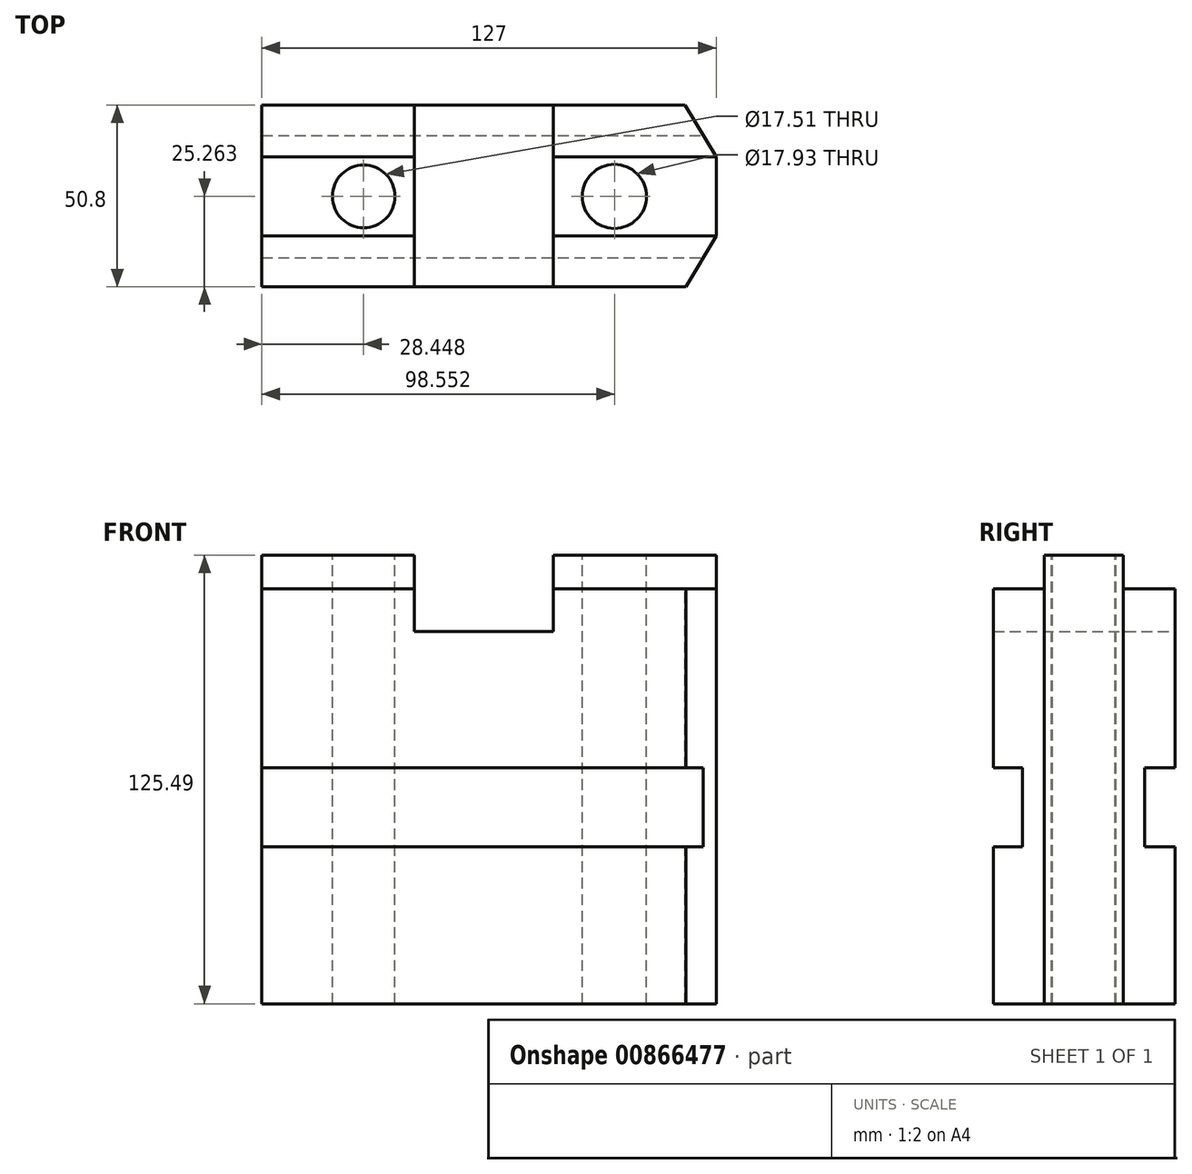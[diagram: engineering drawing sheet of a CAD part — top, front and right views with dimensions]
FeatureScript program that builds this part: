
annotation { "Feature Type Name" : "Feature", "Feature Type Description" : "" }
export const myFeature = defineFeature(function(context is Context, id is Id, definition is map)
    precondition{}
    {
        {
            var Q0;
            Q0=qCreatedBy(makeId("Right.planeOp"),FACE);
            var sketch = newSketch(context, id + "F0", { "sketchPlane" : qUnion([Q0])});
            skLineSegment(sketch, "E0", {"start": v(-42.3, 55.52) * mm, "end": v(-42.3, -60.54) * mm});
            skLineSegment(sketch, "E1", {"start": v(8.5, 55.52) * mm, "end": v(8.5, -60.54) * mm});
            skLineSegment(sketch, "E2", {"start": v(-42.3, 55.52) * mm, "end": v(8.5, 55.52) * mm});
            skLineSegment(sketch, "E3", {"start": v(-42.3, -60.54) * mm, "end": v(8.5, -60.54) * mm});
            skLineSegment(sketch, "E4", {"start": v(-42.3, 55.52) * mm, "end": v(-28.08, 55.52) * mm});
            skLineSegment(sketch, "E5", {"start": v(-28.08, 55.52) * mm, "end": v(-28.08, -60.54) * mm});
            skLineSegment(sketch, "E6", {"start": v(-5.98, 55.52) * mm, "end": v(-5.98, -60.54) * mm});
            skLineSegment(sketch, "E7", {"start": v(-28.08, 55.52) * mm, "end": v(-28.08, 64.95) * mm});
            skLineSegment(sketch, "E8", {"start": v(-5.98, 55.52) * mm, "end": v(-5.98, 64.95) * mm});
            skLineSegment(sketch, "E9", {"start": v(-5.98, 64.95) * mm, "end": v(-28.08, 64.95) * mm});
            skSolve(sketch);
        }
        {
            var Q0;
            {var subQ0=sQuery(id+"F0.wireOp",EDGE,"E7");var subQ1=sQuery(id+"F0.wireOp",EDGE,"E5");var subQ11=makeQuery(id+"F0.imprint","IMPRINT",EDGE,{"derivedFrom":subQ1});var subQ13=sQuery(id+"F0.wireOp",EDGE,"E1");var subQ14=sQuery(id+"F0.wireOp",EDGE,"E0");Q0=qUnion([makeQuery(id+"F0.imprint","IMPRINT",FACE,{"disambiguationData":[TD([[makeQuery(id+"F0.imprint","IMPRINT",EDGE,{"derivedFrom":subQ14}),1.0]])]}),makeQuery(id+"F0.imprint","IMPRINT",FACE,{"disambiguationData":[TD([[makeQuery(id+"F0.imprint","IMPRINT",EDGE,{"derivedFrom":subQ13}),-1.0]])]}),makeQuery(id+"F0.imprint","IMPRINT",FACE,{"disambiguationData":[TD([[makeQuery(id+"F0.imprint","IMPRINT",EDGE,{"derivedFrom":subQ0}),-1.0]])]}),makeQuery(id+"F0.imprint","IMPRINT",FACE,{"disambiguationData":[TD([[subQ11,1.0]])]})]);}
            extrude(context, id + "F1", {"entities" : qUnion([Q0]), "oppositeDirection" : true, "depth" : 127 * mm, "offsetDistance" : 25.4 * mm});
        }
        {
            var Q0;
            Q0=makeQuery(id+"F1.opExtrude","CAP_FACE",FACE,{"disambiguationData":[OSD([sQuery(id+"F0.wireOp",EDGE,"E0"),sQuery(id+"F0.wireOp",EDGE,"E1"),sQuery(id+"F0.wireOp",EDGE,"E2"),sQuery(id+"F0.wireOp",EDGE,"E3"),sQuery(id+"F0.wireOp",EDGE,"E7"),sQuery(id+"F0.wireOp",EDGE,"E8"),sQuery(id+"F0.wireOp",EDGE,"E9")])],"isStart":true});
            var sketch = newSketch(context, id + "F2", { "sketchPlane" : qUnion([Q0])});
            skLineSegment(sketch, "E10.bottom", {"start": v(8.5, 5.46) * mm, "end": v(0, 5.46) * mm});
            skLineSegment(sketch, "E10.top", {"start": v(8.5, -16.64) * mm, "end": v(0, -16.64) * mm});
            skLineSegment(sketch, "E10.left", {"start": v(8.5, 5.46) * mm, "end": v(8.5, -16.64) * mm});
            skLineSegment(sketch, "E10.right", {"start": v(0, 5.46) * mm, "end": v(0, -16.64) * mm});
            skLineSegment(sketch, "E11.bottom", {"start": v(-42.3, 5.46) * mm, "end": v(-34.2, 5.46) * mm});
            skLineSegment(sketch, "E11.top", {"start": v(-42.3, -16.64) * mm, "end": v(-34.2, -16.64) * mm});
            skLineSegment(sketch, "E11.left", {"start": v(-42.3, 5.46) * mm, "end": v(-42.3, -16.64) * mm});
            skLineSegment(sketch, "E11.right", {"start": v(-34.2, 5.46) * mm, "end": v(-34.2, -16.64) * mm});
            skSolve(sketch);
        }
        {
            var Q0;
            Q0=makeQuery(id+"F2.imprint","IMPRINT",FACE,{"disambiguationData":[TD([[makeQuery(id+"F2.imprint","IMPRINT",EDGE,{"derivedFrom":sQuery(id+"F2.wireOp",EDGE,"E10.bottom")}),1.0]])]});
            var Q1;
            Q1=makeQuery(id+"F2.imprint","IMPRINT",FACE,{"disambiguationData":[TD([[makeQuery(id+"F2.imprint","IMPRINT",EDGE,{"derivedFrom":sQuery(id+"F2.wireOp",EDGE,"E11.bottom")}),-1.0]])]});
            extrude(context, id + "F3", {"entities" : qUnion([Q0, Q1]), "operationType" : NewBodyOperationType.REMOVE, "oppositeDirection" : true, "depth" : 254 * mm, "offsetDistance" : 25.4 * mm});
        }
        {
            var Q0;
            Q0=makeQuery(id+"F1.opExtrude","SWEPT_FACE",FACE,{"disambiguationData":[OSD([sQuery(id+"F0.wireOp",EDGE,"E9")])]});
            var sketch = newSketch(context, id + "F4", { "sketchPlane" : qUnion([Q0])});
            skCircle(sketch, "E12", {"center": v(-98.55, -17.03) * mm, "radius": 8.76 * mm});
            skPoint(sketch, "E12.centerSnap0", {"position": v(-127, -17.03) * mm});
            skCircle(sketch, "E13", {"center": v(-28.45, -17.03) * mm, "radius": 8.97 * mm});
            skPoint(sketch, "E13.centerSnap0", {"position": v(0, -17.03) * mm});
            skSolve(sketch);
        }
        {
            var Q0;
            Q0=makeQuery(id+"F4.imprint","IMPRINT",FACE,{"disambiguationData":[TD([[makeQuery(id+"F4.imprint","IMPRINT",EDGE,{"derivedFrom":sQuery(id+"F4.wireOp",EDGE,"E13")}),1.0]])]});
            var Q1;
            Q1=makeQuery(id+"F4.imprint","IMPRINT",FACE,{"disambiguationData":[TD([[makeQuery(id+"F4.imprint","IMPRINT",EDGE,{"derivedFrom":sQuery(id+"F4.wireOp",EDGE,"E12")}),1.0]])]});
            extrude(context, id + "F5", {"entities" : qUnion([Q0, Q1]), "operationType" : NewBodyOperationType.REMOVE, "oppositeDirection" : true, "depth" : 231.14 * mm, "offsetDistance" : 25.4 * mm});
        }
        {
            var Q0;
            {var subQ5=sQuery(id+"F0.wireOp",EDGE,"E1");Q0=makeQuery(id+"F3.boolean.opBoolean","SPLIT",FACE,{"disambiguationData":[TD([makeQuery(id+"F3.opExtrude","SWEPT_FACE",FACE,{"disambiguationData":[OSD([sQuery(id+"F2.wireOp",EDGE,"E10.bottom")])]})])],"derivedFrom":makeQuery(id+"F1.opExtrude","SWEPT_FACE",FACE,{"disambiguationData":[OSD([subQ5])]})});}
            var sketch = newSketch(context, id + "F6", { "sketchPlane" : qUnion([Q0])});
            skLineSegment(sketch, "E14", {"start": v(63.5, 5.46) * mm, "end": v(63.5, 30.86) * mm});
            skLineSegment(sketch, "E15", {"start": v(45.5, 55.52) * mm, "end": v(45.5, 30.86) * mm});
            skLineSegment(sketch, "E16", {"start": v(45.5, 30.86) * mm, "end": v(65.36, 30.86) * mm});
            skLineSegment(sketch, "E17", {"start": v(65.36, 30.86) * mm, "end": v(84.41, 30.86) * mm});
            skLineSegment(sketch, "E18", {"start": v(84.41, 30.86) * mm, "end": v(84.41, 55.52) * mm});
            skLineSegment(sketch, "E19", {"start": v(84.41, 55.52) * mm, "end": v(45.5, 55.52) * mm});
            skSolve(sketch);
        }
        {
            var Q0;
            {var subQ3=sQuery(id+"F6.wireOp",EDGE,"E15");Q0=makeQuery(id+"F6.imprint","IMPRINT",FACE,{"disambiguationData":[TD([[makeQuery(id+"F6.imprint","IMPRINT",EDGE,{"derivedFrom":subQ3}),1.0]])]});}
            extrude(context, id + "F7", {"entities" : qUnion([Q0]), "operationType" : NewBodyOperationType.REMOVE, "oppositeDirection" : true, "depth" : 127 * mm, "offsetDistance" : 25.4 * mm});
        }
        {
            var Q0;
            Q0=makeQuery(id+"F1.opExtrude","SWEPT_FACE",FACE,{"disambiguationData":[OSD([sQuery(id+"F0.wireOp",EDGE,"E8")])]});
            var sketch = newSketch(context, id + "F8", { "sketchPlane" : qUnion([Q0])});
            skLineSegment(sketch, "E20", {"start": v(45.5, 55.52) * mm, "end": v(45.5, 64.95) * mm});
            skLineSegment(sketch, "E21", {"start": v(45.5, 64.95) * mm, "end": v(84.41, 64.95) * mm});
            skLineSegment(sketch, "E22", {"start": v(84.41, 64.95) * mm, "end": v(84.41, 55.52) * mm});
            skSolve(sketch);
        }
        {
            var Q0;
            Q0 = qSketchRegion(id + "F8", true);
            var Q1;
            Q1=makeQuery(id+"F8.imprint","IMPRINT",FACE,{"disambiguationData":[TD([[makeQuery(id+"F8.imprint","IMPRINT",EDGE,{"derivedFrom":sQuery(id+"F8.wireOp",EDGE,"E20")}),-1.0]])]});
            extrude(context, id + "F9", {"entities" : qUnion([Q0, Q1]), "operationType" : NewBodyOperationType.REMOVE, "oppositeDirection" : true, "depth" : 50.8 * mm, "offsetDistance" : 25.4 * mm});
        }
        {
            var Q0;
            Q0=makeQuery(id+"F7.boolean.opBoolean","COPY",FACE,{"derivedFrom":makeQuery(id+"F7.opExtrude","SWEPT_FACE",FACE,{"disambiguationData":[OSD([sQuery(id+"F6.wireOp",EDGE,"E16"),sQuery(id+"F6.wireOp",EDGE,"E17")])]})});
            var sketch = newSketch(context, id + "F10", { "sketchPlane" : qUnion([Q0])});
            skSolve(sketch);
        }
        {
            var Q0;
            Q0 = qSketchRegion(id + "F10", true);
            var Q1;
            {var subQ0=sQuery(id+"F6.wireOp",EDGE,"E16");Q1=makeQuery(id+"F10.imprint","IMPRINT",FACE,{"disambiguationData":[TD([[makeQuery(id+"F10.imprint","IMPRINT",EDGE,{"derivedFrom":makeQuery(id+"F7.boolean.opBoolean","COPY",EDGE,{"derivedFrom":makeQuery(id+"F7.opExtrude","SWEPT_EDGE",EDGE,{"disambiguationData":[OSD([sQuery(id+"F6.wireOp",EDGE,"E15"),subQ0])]})})}),1.0]])]});}
            extrude(context, id + "F11", {"entities" : qUnion([Q0, Q1]), "operationType" : NewBodyOperationType.ADD, "depth" : 12.7 * mm, "offsetDistance" : 25.4 * mm});
        }
        {
            var Q0;
            {var subQ1=sQuery(id+"F0.wireOp",EDGE,"E1");var subQ2=sQuery(id+"F0.wireOp",EDGE,"E2");Q0=makeQuery(id+"F7.boolean.opBoolean","SPLIT",FACE,{"disambiguationData":[TD([makeQuery(id+"F7.opExtrude","SWEPT_FACE",FACE,{"disambiguationData":[OSD([sQuery(id+"F6.wireOp",EDGE,"E15")])]})])],"derivedFrom":makeQuery(id+"F1.opExtrude","SWEPT_FACE",FACE,{"disambiguationData":[OSD([subQ2]),TDD([makeQuery(id+"F0.imprint","IMPRINT",EDGE,{"disambiguationData":[TD([[makeQuery(id+"F0.imprint","INTERSECT",VERTEX,{"derivedFrom":[subQ1,subQ2]}),1.0]])],"derivedFrom":subQ2})])]})});}
            var sketch = newSketch(context, id + "F12", { "sketchPlane" : qUnion([Q0])});
            skLineSegment(sketch, "E23", {"start": v(0, -5.98) * mm, "end": v(-8.7, 8.5) * mm});
            skSolve(sketch);
        }
        {
            var Q0;
            Q0 = qSketchRegion(id + "F12", true);
            var Q1;
            {var subQ0=sQuery(id+"F12.wireOp",EDGE,"E23");Q1=makeQuery(id+"F12.imprint","IMPRINT",FACE,{"disambiguationData":[TD([[makeQuery(id+"F12.imprint","IMPRINT",EDGE,{"derivedFrom":subQ0}),-1.0]])]});}
            extrude(context, id + "F13", {"entities" : qUnion([Q0, Q1]), "operationType" : NewBodyOperationType.REMOVE, "oppositeDirection" : true, "depth" : 254 * mm, "offsetDistance" : 25.4 * mm});
        }
        {
            var Q0;
            {var subQ1=sQuery(id+"F0.wireOp",EDGE,"E0");var subQ2=sQuery(id+"F0.wireOp",EDGE,"E2");Q0=makeQuery(id+"F7.boolean.opBoolean","SPLIT",FACE,{"disambiguationData":[TD([makeQuery(id+"F7.opExtrude","SWEPT_FACE",FACE,{"disambiguationData":[OSD([sQuery(id+"F6.wireOp",EDGE,"E15")])]})])],"derivedFrom":makeQuery(id+"F1.opExtrude","SWEPT_FACE",FACE,{"disambiguationData":[OSD([subQ2]),TDD([makeQuery(id+"F0.imprint","IMPRINT",EDGE,{"disambiguationData":[TD([[makeQuery(id+"F0.imprint","INTERSECT",VERTEX,{"derivedFrom":[subQ1,subQ2]}),-1.0]])],"derivedFrom":subQ2})])]})});}
            var sketch = newSketch(context, id + "F14", { "sketchPlane" : qUnion([Q0])});
            skLineSegment(sketch, "E24", {"start": v(0, -28.08) * mm, "end": v(-8.45, -42.3) * mm});
            skSolve(sketch);
        }
        {
            var Q0;
            {var subQ0=sQuery(id+"F14.wireOp",EDGE,"E24");Q0=makeQuery(id+"F14.imprint","IMPRINT",FACE,{"disambiguationData":[TD([[makeQuery(id+"F14.imprint","IMPRINT",EDGE,{"derivedFrom":subQ0}),1.0]])]});}
            extrude(context, id + "F15", {"entities" : qUnion([Q0]), "operationType" : NewBodyOperationType.REMOVE, "oppositeDirection" : true, "depth" : 128.02 * mm, "offsetDistance" : 25.4 * mm});
        }
    });
